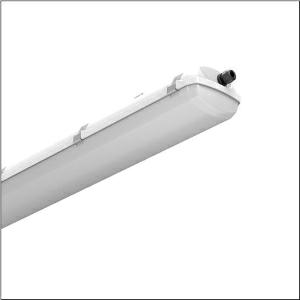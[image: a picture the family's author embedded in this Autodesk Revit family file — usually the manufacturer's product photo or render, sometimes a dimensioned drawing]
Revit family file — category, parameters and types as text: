
# Revit family: monsun_r__ex_51fxb1dp470a_532c
name_source: partatom
category: Lighting Fixtures
units: mm (PartAtom-declared; Revit-internal decimal feet)

## family parameters
Cut with Voids When Loaded = No
Host = Face
Light Source = No
Part Type = Normal
Room Calculation Point = No
Round Connector Dimension = Use Diameter
Shared = No

## types (1)
- Monsun® Ex (1 x LED, 7310 lm, 43.8 W, 4000K)
    Apparent Load = 44 VA
    CIE Flux Codes = 61 86 97 100 100
    Color Rendering = 80
    Color Temperature = 4000K
    Default Elevation = 1800 mm
    Description = Monsun® Ex, damp-proof luminaire, primary optical cover: cover, of PC, UV-stabilised, opal, light emission: direct distribution, primary light characteristic: symmetric, installation type: surface-mounted, LED, rated luminous flux: 7.310lm, luminous efficacy: 167lm/W, light colour: 840, colour temperature: 4000K, control gear: ECG DALI, with terminal, 5-pole, max. 2.5mm², through-wiring: 7x 2.5mm², mains connection: 220..240V, AC, 50/60Hz, rated input power: 44W, housing, of PC, light grey (RAL 7035), incl. blind plug, incl. 1x Ex cable gland M20 for cable diameter 7..12mm with sealing, length: 1.580mm, width: 155mm, height: 105mm, clip for enclosure, of stainless steel, protection rating (complete): IP66, insulation class (complete): insulation class I (protective earthing), certification: CE, explosion class: zone2,22 II 3G Ex nR IIC T6 GC, II 3D Ex tc IIIC T80°C Dc, impact resistance: IK10, permissible operating ambient temperature: -20..+60°C, LABS conformity tested according to VDMA 24364:2018-05, contact your sales advisor before using the luminaires in applications with unclear chemical exposure, large temperature fluctuations or condensation-forming humidity, packaging unit: 1 piece
    Height = 105 mm
    Lamp = 1 x LED
    Lamp Light Flux = 7310 lm
    Lamp Power = 43.8 W
    Lamp count = 1
    Length = 1580 mm
    Luminous efficacy = 167 lm/W
    Manufacturer = Siteco
    ModVariant = No
    Model = 51FXB1DP470A
    Mounting Place = Ceiling
    Mounting Type = Surface mounted
    Number of Poles = 1
    OnlyDefault = Yes
    Power Factor = 1
    Product Name = Monsun® Ex
    Product group = damp-proof luminaire
    ProductGroupID = 301
    Protection Class = Protection class I
    Protection Degree = IP 66
    RLX_Detail_Level = 1
    RLX_Emergency_Light_Flux = 0 lm
    RLX_Emergency_Type = 0
    RLX_Emergency_Type_DB = No
    RlxData = <blob elided: 41637 chars, md5=7bdf6cb1>
    Socket = socket
    Standby Power = 0 W
    System Light Flux = 7310 lm
    System Power = 44 W
    Type Comments = Product without accessories
    Type Image = l_1258882.jpg
    URL = http://relux.com
    VarID = ---
    Voltage = 0 V
    Weight = 0.00 kg
    Width = 155 mm

## geometry (parser evidence)
native form markers: Blend x4, Sweep x9
no freeform markers — native parametric forms only
